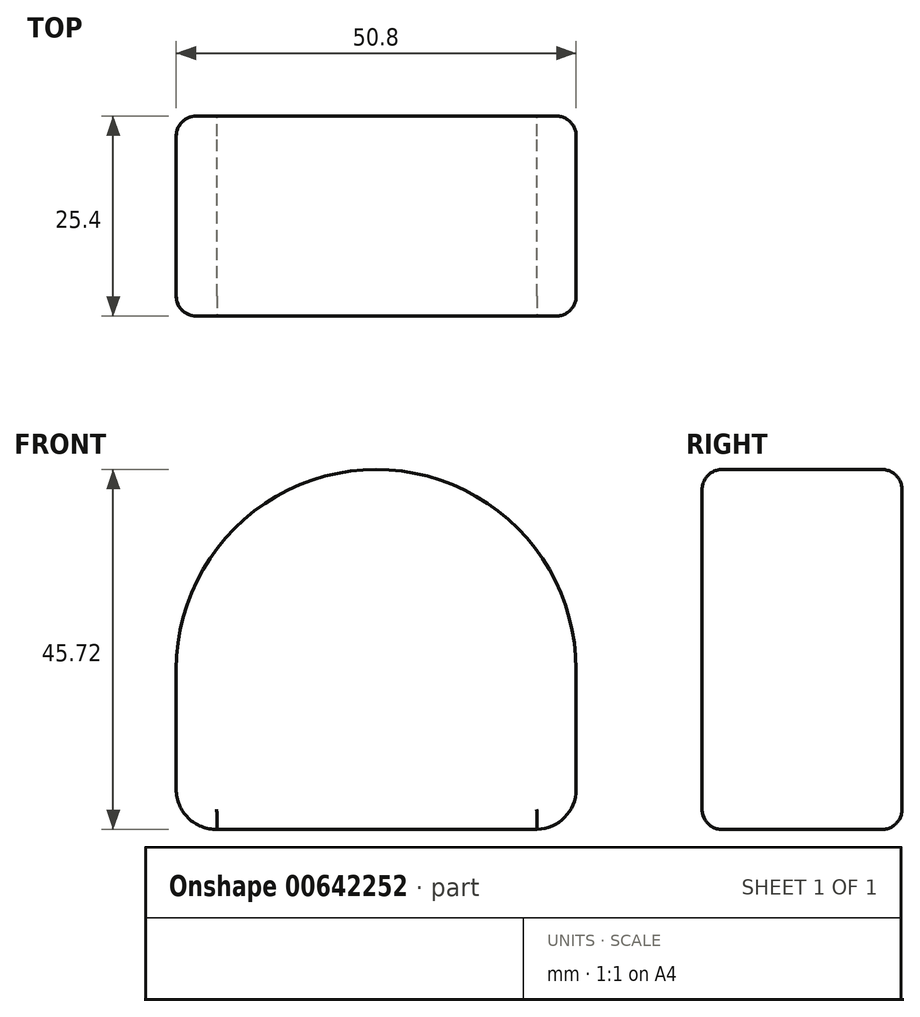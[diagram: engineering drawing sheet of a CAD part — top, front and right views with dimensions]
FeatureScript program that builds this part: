
annotation { "Feature Type Name" : "Feature", "Feature Type Description" : "" }
export const myFeature = defineFeature(function(context is Context, id is Id, definition is map)
    precondition{}
    {
        {
            var Q0;
            Q0=qCreatedBy(makeId("Front.planeOp"),FACE);
            var sketch = newSketch(context, id + "F0", { "sketchPlane" : qUnion([Q0])});
            skArc(sketch, "E0.filletArc", {"start": v(46.24, -2.65) * mm, "mid": v(49.76, -1.13) * mm, "end": v(51.21, 2.43) * mm});
            skPoint(sketch, "E1.visualSharp", {"position": v(0, 0) * mm});
            skArc(sketch, "E1.filletArc", {"start": v(0.41, 2.43) * mm, "mid": v(1.94, -1.2) * mm, "end": v(5.6, -2.65) * mm});
            skLineSegment(sketch, "E2", {"start": v(0.41, 2.43) * mm, "end": v(0.41, 17.67) * mm});
            skLineSegment(sketch, "E3", {"start": v(51.21, 2.43) * mm, "end": v(51.21, 17.67) * mm});
            skArc(sketch, "E4", {"start": v(51.21, 17.67) * mm, "mid": v(25.82, 43.07) * mm, "end": v(0.41, 17.67) * mm});
            skLineSegment(sketch, "E5", {"start": v(5.6, -2.65) * mm, "end": v(46.24, -2.65) * mm});
            skSolve(sketch);
        }
        {
            var Q0;
            Q0=makeQuery(id+"F0.imprint","IMPRINT",FACE,{"disambiguationData":[TD([[makeQuery(id+"F0.imprint","IMPRINT",EDGE,{"derivedFrom":sQuery(id+"F0.wireOp",EDGE,"E0.filletArc")}),1.0]])]});
            extrude(context, id + "F1", {"entities" : qUnion([Q0]), "depth" : 25.4 * mm, "offsetDistance" : 25.4 * mm});
        }
        {
            var Q0;
            Q0=makeQuery(id+"F1.opExtrude","CAP_EDGE",EDGE,{"disambiguationData":[OSD([sQuery(id+"F0.wireOp",EDGE,"E4")])],"isStart":true});
            var Q1;
            Q1=makeQuery(id+"F1.opExtrude","CAP_EDGE",EDGE,{"disambiguationData":[OSD([sQuery(id+"F0.wireOp",EDGE,"E0.filletArc")])],"isStart":true});
            var Q2;
            Q2=makeQuery(id+"F1.opExtrude","CAP_EDGE",EDGE,{"disambiguationData":[OSD([sQuery(id+"F0.wireOp",EDGE,"E3")])],"isStart":true});
            var Q3;
            Q3=makeQuery(id+"F1.opExtrude","CAP_EDGE",EDGE,{"disambiguationData":[OSD([sQuery(id+"F0.wireOp",EDGE,"E3")])],"isStart":false});
            var Q4;
            Q4=makeQuery(id+"F1.opExtrude","CAP_EDGE",EDGE,{"disambiguationData":[OSD([sQuery(id+"F0.wireOp",EDGE,"E0.filletArc")])],"isStart":false});
            var Q5;
            Q5=makeQuery(id+"F1.opExtrude","CAP_EDGE",EDGE,{"disambiguationData":[OSD([sQuery(id+"F0.wireOp",EDGE,"E5")])],"isStart":false});
            var Q6;
            Q6=makeQuery(id+"F1.opExtrude","CAP_EDGE",EDGE,{"disambiguationData":[OSD([sQuery(id+"F0.wireOp",EDGE,"E2")])],"isStart":false});
            var Q7;
            Q7=makeQuery(id+"F1.opExtrude","CAP_EDGE",EDGE,{"disambiguationData":[OSD([sQuery(id+"F0.wireOp",EDGE,"E4")])],"isStart":false});
            var Q8;
            Q8=makeQuery(id+"F1.opExtrude","CAP_EDGE",EDGE,{"disambiguationData":[OSD([sQuery(id+"F0.wireOp",EDGE,"E1.filletArc")])],"isStart":true});
            var Q9;
            Q9=makeQuery(id+"F1.opExtrude","CAP_EDGE",EDGE,{"disambiguationData":[OSD([sQuery(id+"F0.wireOp",EDGE,"E5")])],"isStart":true});
            var Q10;
            Q10=makeQuery(id+"F1.opExtrude","CAP_EDGE",EDGE,{"disambiguationData":[OSD([sQuery(id+"F0.wireOp",EDGE,"E2")])],"isStart":true});
            var Q11;
            Q11=makeQuery(id+"F1.opExtrude","CAP_EDGE",EDGE,{"disambiguationData":[OSD([sQuery(id+"F0.wireOp",EDGE,"E1.filletArc")])],"isStart":false});
            fillet(context, id + "F2", {"entities" : qUnion([Q0, Q1, Q2, Q3, Q4, Q5, Q6, Q7, Q8, Q9, Q10, Q11]), "radius" : 2.54 * mm, "tangentPropagation" : true, "allowEdgeOverflow" : false});
        }
    });
